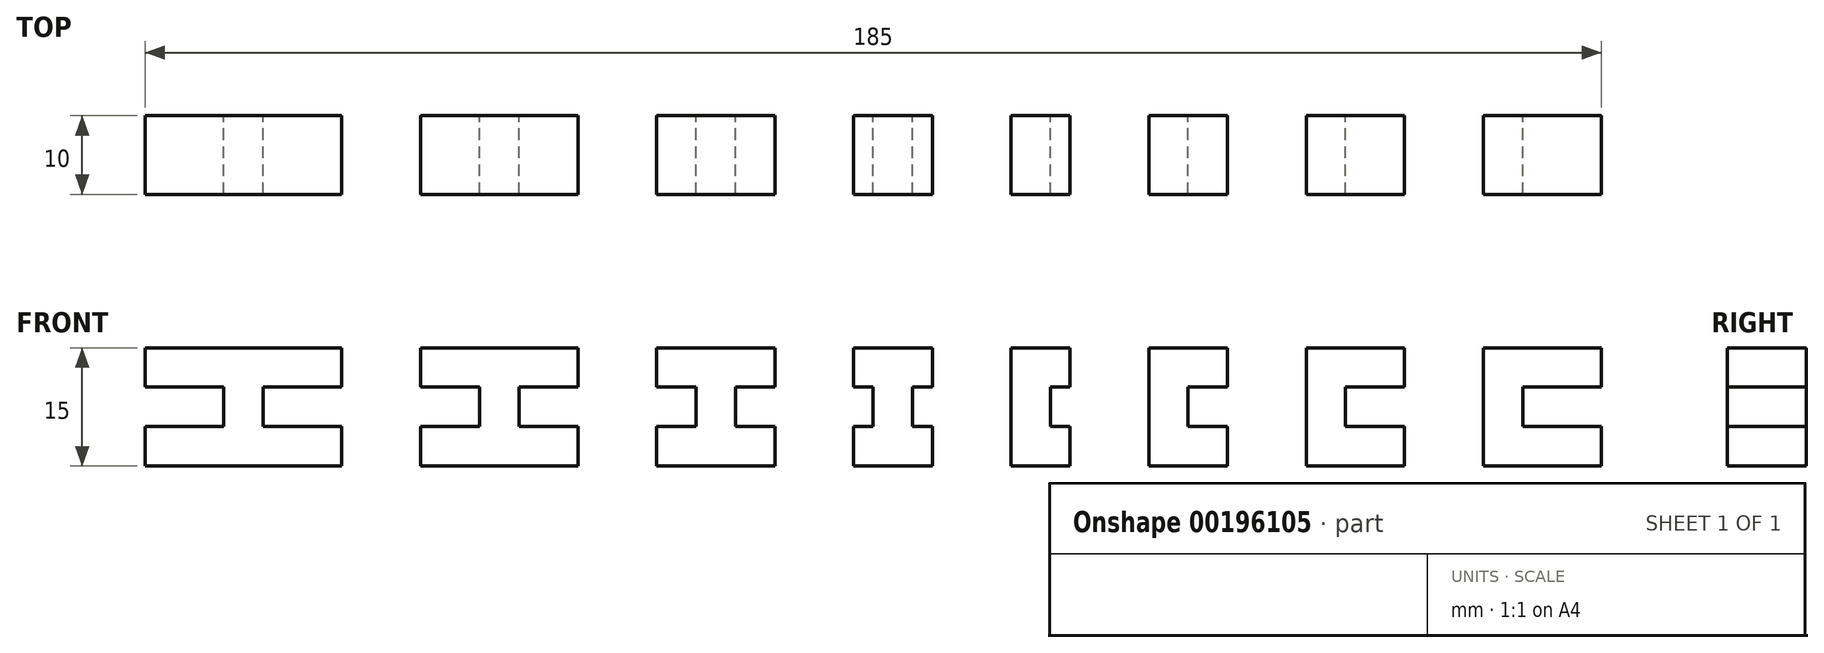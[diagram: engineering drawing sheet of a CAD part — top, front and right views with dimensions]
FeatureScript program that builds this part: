
annotation { "Feature Type Name" : "Feature", "Feature Type Description" : "" }
export const myFeature = defineFeature(function(context is Context, id is Id, definition is map)
    precondition{}
    {
        {
            var Q0;
            Q0=qCreatedBy(makeId("Front.planeOp"),FACE);
            var sketch = newSketch(context, id + "F0", { "sketchPlane" : qUnion([Q0])});
            skLineSegment(sketch, "E0.bottom", {"start": v(5, 15) * mm, "end": v(12.5, 15) * mm});
            skLineSegment(sketch, "E0.top", {"start": v(5, 0) * mm, "end": v(12.5, 0) * mm});
            skLineSegment(sketch, "E0.left", {"start": v(5, 15) * mm, "end": v(5, 0) * mm});
            skLineSegment(sketch, "E1.bottom", {"start": v(12.5, 10) * mm, "end": v(10, 10) * mm});
            skLineSegment(sketch, "E1.top", {"start": v(12.5, 5) * mm, "end": v(10, 5) * mm});
            skLineSegment(sketch, "E1.right", {"start": v(10, 10) * mm, "end": v(10, 5) * mm});
            skLineSegment(sketch, "E2", {"start": v(12.5, 10) * mm, "end": v(12.5, 15) * mm});
            skLineSegment(sketch, "E3", {"start": v(12.5, 5) * mm, "end": v(12.5, 0) * mm});
            skLineSegment(sketch, "E4", {"start": v(0, 0) * mm, "end": v(5, 0) * mm, "construction": true});
            skLineSegment(sketch, "E5.bottom", {"start": v(22.5, 15) * mm, "end": v(32.5, 15) * mm});
            skLineSegment(sketch, "E5.top", {"start": v(22.5, 0) * mm, "end": v(32.5, 0) * mm});
            skLineSegment(sketch, "E5.left", {"start": v(22.5, 15) * mm, "end": v(22.5, 0) * mm});
            skLineSegment(sketch, "E6.bottom", {"start": v(32.5, 10) * mm, "end": v(27.5, 10) * mm});
            skLineSegment(sketch, "E6.top", {"start": v(32.5, 5) * mm, "end": v(27.5, 5) * mm});
            skLineSegment(sketch, "E6.right", {"start": v(27.5, 10) * mm, "end": v(27.5, 5) * mm});
            skLineSegment(sketch, "E7", {"start": v(32.5, 10) * mm, "end": v(32.5, 15) * mm});
            skLineSegment(sketch, "E8", {"start": v(32.5, 5) * mm, "end": v(32.5, 0) * mm});
            skLineSegment(sketch, "E9", {"start": v(12.5, 0) * mm, "end": v(22.5, 0) * mm, "construction": true});
            skLineSegment(sketch, "E10.bottom", {"start": v(42.5, 15) * mm, "end": v(55, 15) * mm});
            skLineSegment(sketch, "E10.top", {"start": v(42.5, 0) * mm, "end": v(55, 0) * mm});
            skLineSegment(sketch, "E10.left", {"start": v(42.5, 15) * mm, "end": v(42.5, 0) * mm});
            skLineSegment(sketch, "E11.bottom", {"start": v(55, 10) * mm, "end": v(47.5, 10) * mm});
            skLineSegment(sketch, "E11.top", {"start": v(55, 5) * mm, "end": v(47.5, 5) * mm});
            skLineSegment(sketch, "E11.right", {"start": v(47.5, 10) * mm, "end": v(47.5, 5) * mm});
            skLineSegment(sketch, "E12", {"start": v(55, 10) * mm, "end": v(55, 15) * mm});
            skLineSegment(sketch, "E13", {"start": v(55, 5) * mm, "end": v(55, 0) * mm});
            skLineSegment(sketch, "E14", {"start": v(32.5, 0) * mm, "end": v(42.5, 0) * mm, "construction": true});
            skLineSegment(sketch, "E15.bottom", {"start": v(65, 15) * mm, "end": v(80, 15) * mm});
            skLineSegment(sketch, "E15.top", {"start": v(65, 0) * mm, "end": v(80, 0) * mm});
            skLineSegment(sketch, "E15.left", {"start": v(65, 15) * mm, "end": v(65, 0) * mm});
            skLineSegment(sketch, "E16.bottom", {"start": v(80, 10) * mm, "end": v(70, 10) * mm});
            skLineSegment(sketch, "E16.top", {"start": v(80, 5) * mm, "end": v(70, 5) * mm});
            skLineSegment(sketch, "E16.right", {"start": v(70, 10) * mm, "end": v(70, 5) * mm});
            skLineSegment(sketch, "E17", {"start": v(80, 10) * mm, "end": v(80, 15) * mm});
            skLineSegment(sketch, "E18", {"start": v(80, 5) * mm, "end": v(80, 0) * mm});
            skLineSegment(sketch, "E19", {"start": v(55, 0) * mm, "end": v(65, 0) * mm, "construction": true});
            skSolve(sketch);
        }
        {
            var Q0;
            Q0=makeQuery(id+"F0.imprint","IMPRINT",FACE,{"disambiguationData":[TD([[makeQuery(id+"F0.imprint","IMPRINT",EDGE,{"derivedFrom":sQuery(id+"F0.wireOp",EDGE,"E0.bottom")}),-1.0]])]});
            var Q1;
            Q1=makeQuery(id+"F0.imprint","IMPRINT",FACE,{"disambiguationData":[TD([[makeQuery(id+"F0.imprint","IMPRINT",EDGE,{"derivedFrom":sQuery(id+"F0.wireOp",EDGE,"E5.bottom")}),-1.0]])]});
            var Q2;
            Q2=makeQuery(id+"F0.imprint","IMPRINT",FACE,{"disambiguationData":[TD([[makeQuery(id+"F0.imprint","IMPRINT",EDGE,{"derivedFrom":sQuery(id+"F0.wireOp",EDGE,"E10.bottom")}),-1.0]])]});
            var Q3;
            Q3=makeQuery(id+"F0.imprint","IMPRINT",FACE,{"disambiguationData":[TD([[makeQuery(id+"F0.imprint","IMPRINT",EDGE,{"derivedFrom":sQuery(id+"F0.wireOp",EDGE,"E15.bottom")}),-1.0]])]});
            extrude(context, id + "F1", {"entities" : qUnion([Q0, Q1, Q2, Q3]), "depth" : 10 * mm});
        }
        {
            var Q0;
            Q0=qCreatedBy(makeId("Front.planeOp"),FACE);
            var sketch = newSketch(context, id + "F2", { "sketchPlane" : qUnion([Q0])});
            skLineSegment(sketch, "E20.bottom", {"start": v(-5, 0) * mm, "end": v(-15, 0) * mm});
            skLineSegment(sketch, "E20.top", {"start": v(-5, 15) * mm, "end": v(-15, 15) * mm});
            skLineSegment(sketch, "E20.left", {"start": v(-5, 0) * mm, "end": v(-5, 5) * mm});
            skLineSegment(sketch, "E20.right", {"start": v(-15, 0) * mm, "end": v(-15, 5) * mm});
            skLineSegment(sketch, "E21.bottom", {"start": v(-15, 10) * mm, "end": v(-12.5, 10) * mm});
            skLineSegment(sketch, "E21.top", {"start": v(-15, 5) * mm, "end": v(-12.5, 5) * mm});
            skLineSegment(sketch, "E21.right", {"start": v(-12.5, 10) * mm, "end": v(-12.5, 5) * mm});
            skLineSegment(sketch, "E22.bottom", {"start": v(-5, 10) * mm, "end": v(-7.5, 10) * mm});
            skLineSegment(sketch, "E22.top", {"start": v(-5, 5) * mm, "end": v(-7.5, 5) * mm});
            skLineSegment(sketch, "E22.right", {"start": v(-7.5, 10) * mm, "end": v(-7.5, 5) * mm});
            skLineSegment(sketch, "E23.trimOffspring", {"start": v(-15, 10) * mm, "end": v(-15, 15) * mm});
            skLineSegment(sketch, "E24.trimOffspring", {"start": v(-5, 10) * mm, "end": v(-5, 15) * mm});
            skLineSegment(sketch, "E25", {"start": v(-5, 0) * mm, "end": v(0, 0) * mm, "construction": true});
            skLineSegment(sketch, "E26.bottom", {"start": v(-25, 0) * mm, "end": v(-40, 0) * mm});
            skLineSegment(sketch, "E26.top", {"start": v(-25, 15) * mm, "end": v(-40, 15) * mm});
            skLineSegment(sketch, "E26.left", {"start": v(-25, 0) * mm, "end": v(-25, 5) * mm});
            skLineSegment(sketch, "E26.right", {"start": v(-40, 0) * mm, "end": v(-40, 5) * mm});
            skLineSegment(sketch, "E27.bottom", {"start": v(-40, 10) * mm, "end": v(-35, 10) * mm});
            skLineSegment(sketch, "E27.top", {"start": v(-40, 5) * mm, "end": v(-35, 5) * mm});
            skLineSegment(sketch, "E27.right", {"start": v(-35, 10) * mm, "end": v(-35, 5) * mm});
            skLineSegment(sketch, "E28.bottom", {"start": v(-25, 10) * mm, "end": v(-30, 10) * mm});
            skLineSegment(sketch, "E28.top", {"start": v(-25, 5) * mm, "end": v(-30, 5) * mm});
            skLineSegment(sketch, "E28.right", {"start": v(-30, 10) * mm, "end": v(-30, 5) * mm});
            skLineSegment(sketch, "E29.trimOffspring", {"start": v(-40, 10) * mm, "end": v(-40, 15) * mm});
            skLineSegment(sketch, "E30.trimOffspring", {"start": v(-25, 10) * mm, "end": v(-25, 15) * mm});
            skLineSegment(sketch, "E31", {"start": v(-25, 0) * mm, "end": v(-15, 0) * mm, "construction": true});
            skLineSegment(sketch, "E32.bottom", {"start": v(-50, 0) * mm, "end": v(-70, 0) * mm});
            skLineSegment(sketch, "E32.top", {"start": v(-50, 15) * mm, "end": v(-70, 15) * mm});
            skLineSegment(sketch, "E32.left", {"start": v(-50, 0) * mm, "end": v(-50, 5) * mm});
            skLineSegment(sketch, "E32.right", {"start": v(-70, 0) * mm, "end": v(-70, 5) * mm});
            skLineSegment(sketch, "E33.bottom", {"start": v(-70, 10) * mm, "end": v(-62.5, 10) * mm});
            skLineSegment(sketch, "E33.top", {"start": v(-70, 5) * mm, "end": v(-62.5, 5) * mm});
            skLineSegment(sketch, "E33.right", {"start": v(-62.5, 10) * mm, "end": v(-62.5, 5) * mm});
            skLineSegment(sketch, "E34.bottom", {"start": v(-50, 10) * mm, "end": v(-57.5, 10) * mm});
            skLineSegment(sketch, "E34.top", {"start": v(-50, 5) * mm, "end": v(-57.5, 5) * mm});
            skLineSegment(sketch, "E34.right", {"start": v(-57.5, 10) * mm, "end": v(-57.5, 5) * mm});
            skLineSegment(sketch, "E35.trimOffspring", {"start": v(-70, 10) * mm, "end": v(-70, 15) * mm});
            skLineSegment(sketch, "E36.trimOffspring", {"start": v(-50, 10) * mm, "end": v(-50, 15) * mm});
            skLineSegment(sketch, "E37", {"start": v(-50, 0) * mm, "end": v(-40, 0) * mm, "construction": true});
            skLineSegment(sketch, "E38.bottom", {"start": v(-80, 0) * mm, "end": v(-105, 0) * mm});
            skLineSegment(sketch, "E38.top", {"start": v(-80, 15) * mm, "end": v(-105, 15) * mm});
            skLineSegment(sketch, "E38.left", {"start": v(-80, 0) * mm, "end": v(-80, 5) * mm});
            skLineSegment(sketch, "E38.right", {"start": v(-105, 0) * mm, "end": v(-105, 5) * mm});
            skLineSegment(sketch, "E39.bottom", {"start": v(-105, 10) * mm, "end": v(-95, 10) * mm});
            skLineSegment(sketch, "E39.top", {"start": v(-105, 5) * mm, "end": v(-95, 5) * mm});
            skLineSegment(sketch, "E39.right", {"start": v(-95, 10) * mm, "end": v(-95, 5) * mm});
            skLineSegment(sketch, "E40.bottom", {"start": v(-80, 10) * mm, "end": v(-90, 10) * mm});
            skLineSegment(sketch, "E40.top", {"start": v(-80, 5) * mm, "end": v(-90, 5) * mm});
            skLineSegment(sketch, "E40.right", {"start": v(-90, 10) * mm, "end": v(-90, 5) * mm});
            skLineSegment(sketch, "E41.trimOffspring", {"start": v(-105, 10) * mm, "end": v(-105, 15) * mm});
            skLineSegment(sketch, "E42.trimOffspring", {"start": v(-80, 10) * mm, "end": v(-80, 15) * mm});
            skLineSegment(sketch, "E43", {"start": v(-80, 0) * mm, "end": v(-70, 0) * mm, "construction": true});
            skSolve(sketch);
        }
        {
            var Q0;
            Q0=makeQuery(id+"F2.imprint","IMPRINT",FACE,{"disambiguationData":[TD([[makeQuery(id+"F2.imprint","IMPRINT",EDGE,{"derivedFrom":sQuery(id+"F2.wireOp",EDGE,"E38.bottom")}),-1.0]])]});
            var Q1;
            Q1=makeQuery(id+"F2.imprint","IMPRINT",FACE,{"disambiguationData":[TD([[makeQuery(id+"F2.imprint","IMPRINT",EDGE,{"derivedFrom":sQuery(id+"F2.wireOp",EDGE,"E32.bottom")}),-1.0]])]});
            var Q2;
            Q2=makeQuery(id+"F2.imprint","IMPRINT",FACE,{"disambiguationData":[TD([[makeQuery(id+"F2.imprint","IMPRINT",EDGE,{"derivedFrom":sQuery(id+"F2.wireOp",EDGE,"E26.bottom")}),-1.0]])]});
            var Q3;
            Q3=makeQuery(id+"F2.imprint","IMPRINT",FACE,{"disambiguationData":[TD([[makeQuery(id+"F2.imprint","IMPRINT",EDGE,{"derivedFrom":sQuery(id+"F2.wireOp",EDGE,"E20.bottom")}),-1.0]])]});
            extrude(context, id + "F3", {"entities" : qUnion([Q0, Q1, Q2, Q3]), "depth" : 10 * mm});
        }
    });
